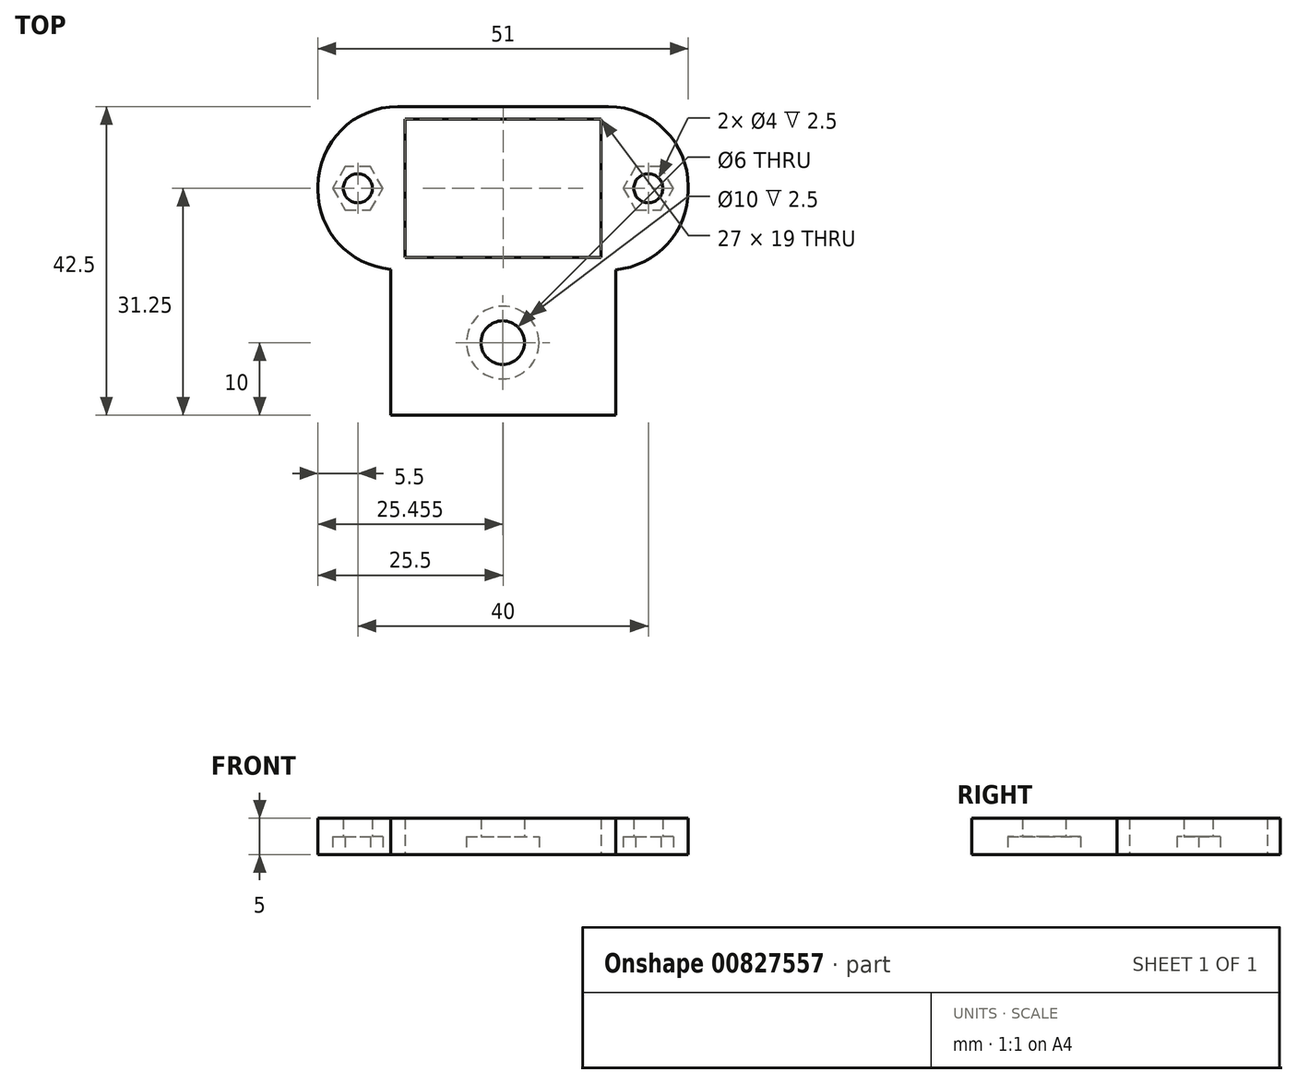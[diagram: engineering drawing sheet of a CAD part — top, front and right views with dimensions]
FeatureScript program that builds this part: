
annotation { "Feature Type Name" : "Feature", "Feature Type Description" : "" }
export const myFeature = defineFeature(function(context is Context, id is Id, definition is map)
    precondition{}
    {
        {
            var Q0;
            Q0=qCreatedBy(makeId("Top.planeOp"),FACE);
            var sketch = newSketch(context, id + "F0", { "sketchPlane" : qUnion([Q0])});
            skLineSegment(sketch, "E0.bottom", {"start": v(13.5, 9.5) * mm, "end": v(-13.5, 9.5) * mm});
            skLineSegment(sketch, "E0.top", {"start": v(13.5, -9.5) * mm, "end": v(-13.5, -9.5) * mm});
            skLineSegment(sketch, "E0.left", {"start": v(13.5, 9.5) * mm, "end": v(13.5, -9.5) * mm});
            skLineSegment(sketch, "E0.right", {"start": v(-13.5, 9.5) * mm, "end": v(-13.5, -9.5) * mm});
            skPoint(sketch, "E0.middle", {"position": v(0, 0) * mm});
            skLineSegment(sketch, "E1.bottom", {"start": v(15.5, 11.25) * mm, "end": v(-15.5, 11.25) * mm});
            skLineSegment(sketch, "E1.top", {"start": v(15.5, -11.25) * mm, "end": v(-15.5, -11.25) * mm});
            skLineSegment(sketch, "E1.left", {"start": v(15.5, 11.25) * mm, "end": v(15.5, -11.25) * mm});
            skLineSegment(sketch, "E1.right", {"start": v(-15.5, 11.25) * mm, "end": v(-15.5, -11.25) * mm});
            skSolve(sketch);
        }
        {
            var Q0;
            Q0 = qSketchRegion(id + "F0", true);
            extrude(context, id + "F1", {"entities" : qUnion([Q0]), "depth" : 5 * mm, "offsetDistance" : 25 * mm});
        }
        {
            var Q0;
            Q0=makeQuery(id+"F1.opExtrude","SWEPT_FACE",FACE,{"disambiguationData":[OSD([sQuery(id+"F0.wireOp",EDGE,"E1.top")])]});
            extrude(context, id + "F2", {"entities" : qUnion([Q0]), "operationType" : NewBodyOperationType.ADD, "depth" : 20 * mm, "offsetDistance" : 25 * mm});
        }
        {
            var Q0;
            {var subQ0=sQuery(id+"F0.wireOp",EDGE,"E1.left");Q0=makeQuery(id+"F2.boolean.opBoolean","MERGE",FACE,{"derivedFrom":[makeQuery(id+"F1.opExtrude","SWEPT_FACE",FACE,{"disambiguationData":[OSD([subQ0])]}),makeQuery(id+"F2.opExtrude","SWEPT_FACE",FACE,{"disambiguationData":[OSD([sQuery(id+"F0.wireOp",EDGE,"E1.top"),subQ0])]})]});}
            var sketch = newSketch(context, id + "F3", { "sketchPlane" : qUnion([Q0])});
            skLineSegment(sketch, "E2", {"start": v(-11.21, 0) * mm, "end": v(-11.21, 5) * mm});
            skSolve(sketch);
        }
        {
            var Q0;
            {var subQ0=sQuery(id+"F3.wireOp",EDGE,"E2");Q0=makeQuery(id+"F3.imprint","IMPRINT",FACE,{"disambiguationData":[TD([[makeQuery(id+"F3.imprint","IMPRINT",EDGE,{"derivedFrom":subQ0}),-1.0]])]});}
            extrude(context, id + "F4", {"entities" : qUnion([Q0]), "operationType" : NewBodyOperationType.ADD, "depth" : 10 * mm, "offsetDistance" : 25 * mm});
        }
        {
            var Q0;
            {var subQ0=sQuery(id+"F0.wireOp",EDGE,"E1.right");Q0=makeQuery(id+"F2.boolean.opBoolean","MERGE",FACE,{"derivedFrom":[makeQuery(id+"F1.opExtrude","SWEPT_FACE",FACE,{"disambiguationData":[OSD([subQ0])]}),makeQuery(id+"F2.opExtrude","SWEPT_FACE",FACE,{"disambiguationData":[OSD([sQuery(id+"F0.wireOp",EDGE,"E1.top"),subQ0])]})]});}
            var sketch = newSketch(context, id + "F5", { "sketchPlane" : qUnion([Q0])});
            skLineSegment(sketch, "E3", {"start": v(11.15, 0) * mm, "end": v(11.15, 5) * mm});
            skSolve(sketch);
        }
        {
            var Q0;
            {var subQ0=sQuery(id+"F5.wireOp",EDGE,"E3");Q0=makeQuery(id+"F5.imprint","IMPRINT",FACE,{"disambiguationData":[TD([[makeQuery(id+"F5.imprint","IMPRINT",EDGE,{"derivedFrom":subQ0}),1.0]])]});}
            extrude(context, id + "F6", {"entities" : qUnion([Q0]), "operationType" : NewBodyOperationType.ADD, "depth" : 10 * mm, "offsetDistance" : 25 * mm});
        }
        {
            var Q0;
            {var subQ0=sQuery(id+"F0.wireOp",EDGE,"E1.right");var subQ1=sQuery(id+"F0.wireOp",EDGE,"E1.top");var subQ2=makeQuery(id+"F2.boolean.opBoolean","MERGE",EDGE,{"derivedFrom":[makeQuery(id+"F1.opExtrude","CAP_EDGE",EDGE,{"disambiguationData":[OSD([subQ0])],"isStart":true}),makeQuery(id+"F2.opExtrude","SWEPT_EDGE",EDGE,{"disambiguationData":[OSD([subQ1,subQ0]),TDD([makeQuery(id+"F1.opExtrude","CAP_VERTEX",VERTEX,{"disambiguationData":[OSD([subQ1,subQ0])],"isStart":true})])]})]});var subQ3=sQuery(id+"F0.wireOp",EDGE,"E1.bottom");var subQ4=sQuery(id+"F0.wireOp",EDGE,"E1.left");var subQ5=makeQuery(id+"F2.boolean.opBoolean","MERGE",EDGE,{"derivedFrom":[makeQuery(id+"F1.opExtrude","CAP_EDGE",EDGE,{"disambiguationData":[OSD([subQ4])],"isStart":true}),makeQuery(id+"F2.opExtrude","SWEPT_EDGE",EDGE,{"disambiguationData":[OSD([subQ1,subQ4]),TDD([makeQuery(id+"F1.opExtrude","CAP_VERTEX",VERTEX,{"disambiguationData":[OSD([subQ1,subQ4])],"isStart":true})])]})]});Q0=makeQuery(id+"F6.boolean.opBoolean","MERGE",FACE,{"derivedFrom":[makeQuery(id+"F4.boolean.opBoolean","MERGE",FACE,{"derivedFrom":[makeQuery(id+"F2.boolean.opBoolean","MERGE",FACE,{"derivedFrom":[makeQuery(id+"F1.opExtrude","CAP_FACE",FACE,{"disambiguationData":[OSD([sQuery(id+"F0.wireOp",EDGE,"E0.bottom"),sQuery(id+"F0.wireOp",EDGE,"E0.top"),sQuery(id+"F0.wireOp",EDGE,"E0.left"),sQuery(id+"F0.wireOp",EDGE,"E0.right"),subQ3,subQ1,subQ4,subQ0])],"isStart":true}),makeQuery(id+"F2.opExtrude","SWEPT_FACE",FACE,{"disambiguationData":[OSD([subQ1]),TDD([makeQuery(id+"F1.opExtrude","CAP_EDGE",EDGE,{"disambiguationData":[OSD([subQ1])],"isStart":true})])]})]}),makeQuery(id+"F4.opExtrude","SWEPT_FACE",FACE,{"disambiguationData":[OSD([subQ1,subQ4]),TDD([makeQuery(id+"F3.imprint","IMPRINT",EDGE,{"disambiguationData":[TD([[makeQuery(id+"F3.imprint","INTERSECT",VERTEX,{"derivedFrom":[subQ5,sQuery(id+"F3.wireOp",EDGE,"E2")]}),1.0]])],"derivedFrom":subQ5})])]})]}),makeQuery(id+"F6.opExtrude","SWEPT_FACE",FACE,{"disambiguationData":[OSD([subQ1,subQ0]),TDD([makeQuery(id+"F5.imprint","IMPRINT",EDGE,{"disambiguationData":[TD([[makeQuery(id+"F5.imprint","INTERSECT",VERTEX,{"derivedFrom":[subQ2,sQuery(id+"F5.wireOp",EDGE,"E3")]}),1.0]])],"derivedFrom":subQ2})])]})]});}
            var sketch = newSketch(context, id + "F7", { "sketchPlane" : qUnion([Q0])});
            skLineSegment(sketch, "E4", {"start": v(21.85, 21.25) * mm, "end": v(-21.94, 21.25) * mm, "construction": true});
            skCircle(sketch, "E5", {"center": v(-0.04, 21.25) * mm, "radius": 3 * mm});
            skCircle(sketch, "E6.0", {"center": v(-0.04, 21.25) * mm, "radius": 5 * mm});
            skLineSegment(sketch, "E7", {"start": v(20, -15.4) * mm, "end": v(20, 15.4) * mm, "construction": true});
            skLineSegment(sketch, "E8", {"start": v(-20, -15.8) * mm, "end": v(-20, 15.8) * mm, "construction": true});
            skCircle(sketch, "E9", {"center": v(20, 0) * mm, "radius": 2 * mm});
            skCircle(sketch, "E10", {"center": v(-20, 0) * mm, "radius": 2 * mm});
            skCircle(sketch, "E11.cCircle", {"center": v(20, 0) * mm, "radius": 3 * mm, "construction": true});
            skLineSegment(sketch, "E11.0", {"start": v(18.27, 3) * mm, "end": v(21.73, 3) * mm});
            skLineSegment(sketch, "E11.1", {"start": v(21.73, 3) * mm, "end": v(23.46, 0) * mm});
            skLineSegment(sketch, "E11.2", {"start": v(23.46, 0) * mm, "end": v(21.73, -3) * mm});
            skLineSegment(sketch, "E11.3", {"start": v(21.73, -3) * mm, "end": v(18.27, -3) * mm});
            skLineSegment(sketch, "E11.4", {"start": v(18.27, -3) * mm, "end": v(16.54, 0) * mm});
            skLineSegment(sketch, "E11.5", {"start": v(16.54, 0) * mm, "end": v(18.27, 3) * mm});
            skPoint(sketch, "E11.0.midPoint", {"position": v(20, 3) * mm});
            skCircle(sketch, "E12.cCircle", {"center": v(-20, 0) * mm, "radius": 3 * mm, "construction": true});
            skLineSegment(sketch, "E12.0", {"start": v(-21.73, 3) * mm, "end": v(-18.27, 3) * mm});
            skLineSegment(sketch, "E12.1", {"start": v(-18.27, 3) * mm, "end": v(-16.54, 0) * mm});
            skLineSegment(sketch, "E12.2", {"start": v(-16.54, 0) * mm, "end": v(-18.27, -3) * mm});
            skLineSegment(sketch, "E12.3", {"start": v(-18.27, -3) * mm, "end": v(-21.73, -3) * mm});
            skLineSegment(sketch, "E12.4", {"start": v(-21.73, -3) * mm, "end": v(-23.46, 0) * mm});
            skLineSegment(sketch, "E12.5", {"start": v(-23.46, 0) * mm, "end": v(-21.73, 3) * mm});
            skPoint(sketch, "E12.0.midPoint", {"position": v(-20, 3) * mm});
            skLineSegment(sketch, "E13", {"start": v(-36.8, 0) * mm, "end": v(41.61, 0) * mm, "construction": true});
            skSolve(sketch);
        }
        {
            var Q0;
            Q0=makeQuery(id+"F7.imprint","IMPRINT",FACE,{"disambiguationData":[TD([[makeQuery(id+"F7.imprint","IMPRINT",EDGE,{"derivedFrom":sQuery(id+"F7.wireOp",EDGE,"E5")}),1.0]])]});
            var Q1;
            Q1=makeQuery(id+"F7.imprint","IMPRINT",FACE,{"disambiguationData":[TD([[makeQuery(id+"F7.imprint","IMPRINT",EDGE,{"derivedFrom":sQuery(id+"F7.wireOp",EDGE,"E9")}),1.0]])]});
            var Q2;
            Q2=makeQuery(id+"F7.imprint","IMPRINT",FACE,{"disambiguationData":[TD([[makeQuery(id+"F7.imprint","IMPRINT",EDGE,{"derivedFrom":sQuery(id+"F7.wireOp",EDGE,"E10")}),1.0]])]});
            extrude(context, id + "F8", {"entities" : qUnion([Q0, Q1, Q2]), "operationType" : NewBodyOperationType.REMOVE, "oppositeDirection" : true, "depth" : 25 * mm, "offsetDistance" : 25 * mm});
        }
        {
            var Q0;
            Q0=makeQuery(id+"F7.imprint","IMPRINT",FACE,{"disambiguationData":[TD([[makeQuery(id+"F7.imprint","IMPRINT",EDGE,{"derivedFrom":sQuery(id+"F7.wireOp",EDGE,"E5")}),-1.0]])]});
            var Q1;
            Q1=makeQuery(id+"F7.imprint","IMPRINT",FACE,{"disambiguationData":[TD([[makeQuery(id+"F7.imprint","IMPRINT",EDGE,{"derivedFrom":sQuery(id+"F7.wireOp",EDGE,"E9")}),-1.0]])]});
            var Q2;
            Q2=makeQuery(id+"F7.imprint","IMPRINT",FACE,{"disambiguationData":[TD([[makeQuery(id+"F7.imprint","IMPRINT",EDGE,{"derivedFrom":sQuery(id+"F7.wireOp",EDGE,"E10")}),-1.0]])]});
            extrude(context, id + "F9", {"entities" : qUnion([Q0, Q1, Q2]), "operationType" : NewBodyOperationType.REMOVE, "oppositeDirection" : true, "depth" : 2.5 * mm, "offsetDistance" : 25 * mm});
        }
        {
            var Q0;
            Q0=makeQuery(id+"F6.opExtrude","CAP_EDGE",EDGE,{"disambiguationData":[OSD([sQuery(id+"F0.wireOp",EDGE,"E1.bottom"),sQuery(id+"F0.wireOp",EDGE,"E1.right")])],"isStart":false});
            var Q1;
            Q1=makeQuery(id+"F6.opExtrude","CAP_EDGE",EDGE,{"disambiguationData":[OSD([sQuery(id+"F5.wireOp",EDGE,"E3")])],"isStart":false});
            var Q2;
            Q2=makeQuery(id+"F4.opExtrude","CAP_EDGE",EDGE,{"disambiguationData":[OSD([sQuery(id+"F3.wireOp",EDGE,"E2")])],"isStart":false});
            var Q3;
            Q3=makeQuery(id+"F4.opExtrude","CAP_EDGE",EDGE,{"disambiguationData":[OSD([sQuery(id+"F0.wireOp",EDGE,"E1.bottom"),sQuery(id+"F0.wireOp",EDGE,"E1.left")])],"isStart":false});
            fillet(context, id + "F10", {"entities" : qUnion([Q0, Q1, Q2, Q3]), "radius" : 11 * mm, "tangentPropagation" : true, "allowEdgeOverflow" : false});
        }
    });
